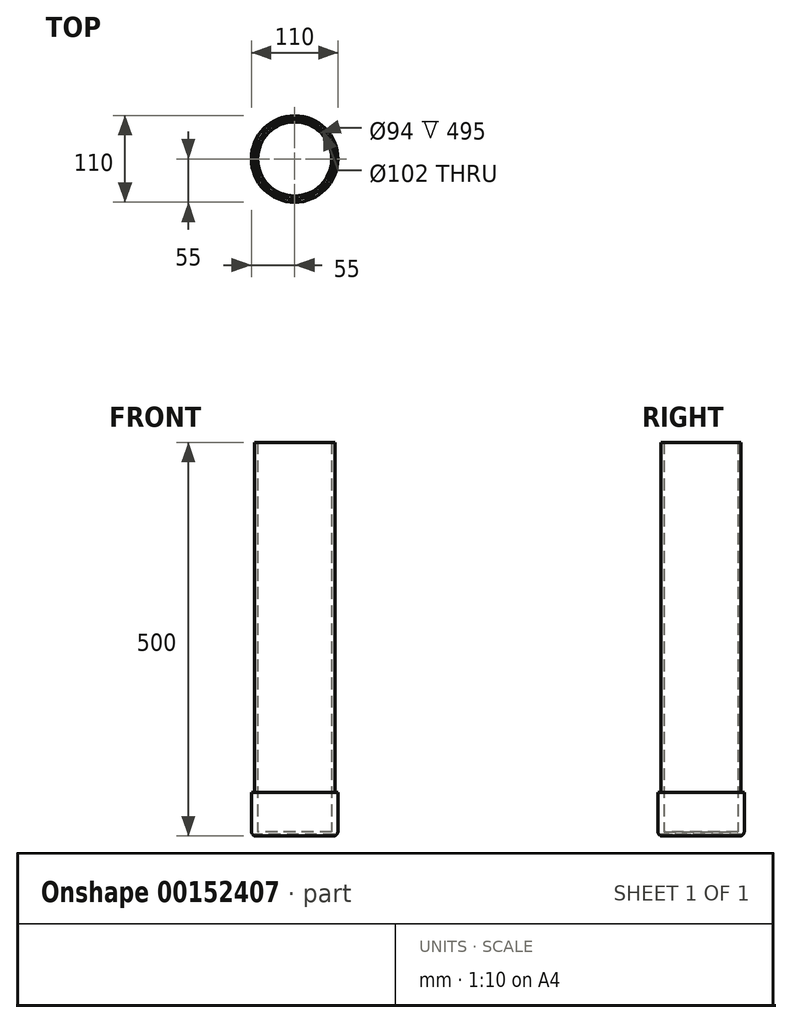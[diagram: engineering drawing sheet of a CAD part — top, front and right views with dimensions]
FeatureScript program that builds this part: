
annotation { "Feature Type Name" : "Feature", "Feature Type Description" : "" }
export const myFeature = defineFeature(function(context is Context, id is Id, definition is map)
    precondition{}
    {
        {
            var Q0;
            Q0=qCreatedBy(makeId("Top.planeOp"),FACE);
            var sketch = newSketch(context, id + "F0", { "sketchPlane" : qUnion([Q0])});
            skCircle(sketch, "E0", {"center": v(0, 0) * mm, "radius": 51 * mm});
            skCircle(sketch, "E1", {"center": v(0, 0) * mm, "radius": 47 * mm});
            skCircle(sketch, "E2", {"center": v(0, 0) * mm, "radius": 55 * mm});
            skSolve(sketch);
        }
        {
            var Q0;
            Q0=makeQuery(id+"F0.imprint","IMPRINT",FACE,{"disambiguationData":[TD([[makeQuery(id+"F0.imprint","IMPRINT",EDGE,{"derivedFrom":sQuery(id+"F0.wireOp",EDGE,"E0")}),-1.0]])]});
            var Q1;
            Q1=makeQuery(id+"F0.imprint","IMPRINT",FACE,{"disambiguationData":[TD([[makeQuery(id+"F0.imprint","IMPRINT",EDGE,{"derivedFrom":sQuery(id+"F0.wireOp",EDGE,"E0")}),1.0]])]});
            var Q2;
            Q2=makeQuery(id+"F0.imprint","IMPRINT",FACE,{"disambiguationData":[TD([[makeQuery(id+"F0.imprint","IMPRINT",EDGE,{"derivedFrom":sQuery(id+"F0.wireOp",EDGE,"E1")}),1.0]])]});
            extrude(context, id + "F1", {"entities" : qUnion([Q0, Q1, Q2]), "depth" : 5 * mm});
        }
        {
            var Q0;
            Q0=makeQuery(id+"F0.imprint","IMPRINT",FACE,{"disambiguationData":[TD([[makeQuery(id+"F0.imprint","IMPRINT",EDGE,{"derivedFrom":sQuery(id+"F0.wireOp",EDGE,"E0")}),1.0]])]});
            extrude(context, id + "F2", {"entities" : qUnion([Q0]), "operationType" : NewBodyOperationType.ADD, "depth" : 500 * mm});
        }
        {
            var Q0;
            {var subQ0=sQuery(id+"F0.wireOp",EDGE,"E2");Q0=makeQuery(id+"F2.boolean.opBoolean","SPLIT",FACE,{"disambiguationData":[TD([makeQuery(id+"F1.opExtrude","SWEPT_FACE",FACE,{"disambiguationData":[OSD([subQ0])]})])],"derivedFrom":makeQuery(id+"F1.opExtrude","CAP_FACE",FACE,{"disambiguationData":[OSD([subQ0])],"isStart":false})});}
            extrude(context, id + "F3", {"entities" : qUnion([Q0]), "operationType" : NewBodyOperationType.ADD, "depth" : 50 * mm});
        }
        {
            var Q0;
            Q0=makeQuery(id+"F1.opExtrude","CAP_EDGE",EDGE,{"disambiguationData":[OSD([sQuery(id+"F0.wireOp",EDGE,"E2")])],"isStart":true});
            fillet(context, id + "F4", {"entities" : qUnion([Q0]), "radius" : 10 * mm, "tangentPropagation" : true, "allowEdgeOverflow" : false});
        }
        {
            var Q0;
            Q0=qSketchRegion(id+"F0",true);
            extrude(context, id + "F5", {"entities" : qUnion([Q0]), "operationType" : NewBodyOperationType.ADD, "depth" : 25 * mm});
        }
        {
            var Q0;
            Q0=qSketchRegion(id+"F0",true);
            extrude(context, id + "F6", {"entities" : qUnion([Q0]), "operationType" : NewBodyOperationType.ADD, "depth" : 25 * mm});
        }
        {
            var Q0;
            Q0=qSketchRegion(id+"F0",true);
            extrude(context, id + "F7", {"entities" : qUnion([Q0]), "operationType" : NewBodyOperationType.ADD, "depth" : 25 * mm});
        }
        {
            var Q0;
            Q0=makeQuery(id+"F5.opExtrude","CAP_EDGE",EDGE,{"disambiguationData":[OSD([sQuery(id+"F0.wireOp",EDGE,"E2")])],"isStart":true});
            fillet(context, id + "F8", {"entities" : qUnion([Q0]), "radius" : 7 * mm, "tangentPropagation" : true, "allowEdgeOverflow" : false});
        }
    });
